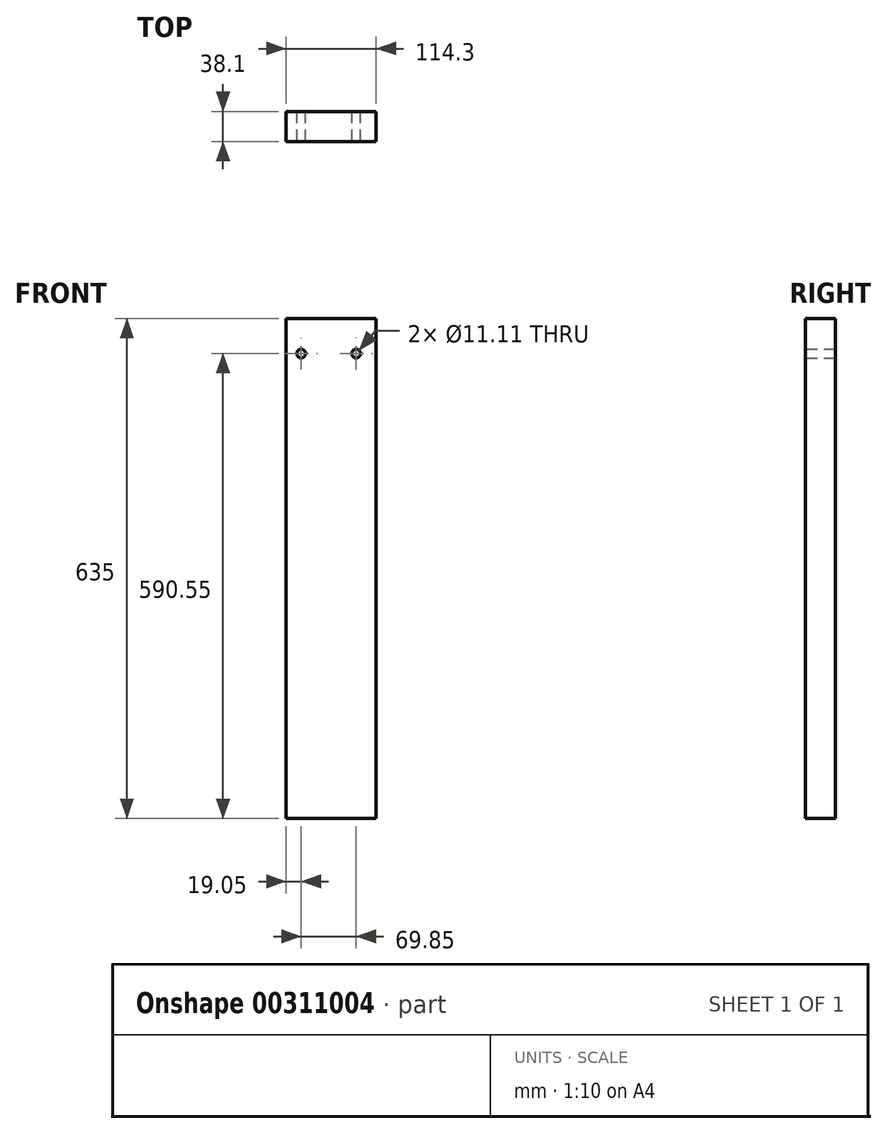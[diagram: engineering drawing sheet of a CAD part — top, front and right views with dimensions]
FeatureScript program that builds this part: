
annotation { "Feature Type Name" : "Feature", "Feature Type Description" : "" }
export const myFeature = defineFeature(function(context is Context, id is Id, definition is map)
    precondition{}
    {
        {
            var Q0;
            Q0=qCreatedBy(makeId("Front.planeOp"),FACE);
            var sketch = newSketch(context, id + "F0", { "sketchPlane" : qUnion([Q0])});
            skLineSegment(sketch, "E0", {"start": v(0, 0) * mm, "end": v(114.3, 0) * mm});
            skLineSegment(sketch, "E1", {"start": v(114.3, 0) * mm, "end": v(114.3, -635) * mm});
            skLineSegment(sketch, "E2", {"start": v(114.3, -635) * mm, "end": v(0, -635) * mm});
            skLineSegment(sketch, "E3", {"start": v(0, -635) * mm, "end": v(0, 0) * mm});
            skSolve(sketch);
        }
        {
            var Q0;
            Q0=makeQuery(id+"F0.imprint","IMPRINT",FACE,{"disambiguationData":[TD([[makeQuery(id+"F0.imprint","IMPRINT",EDGE,{"derivedFrom":sQuery(id+"F0.wireOp",EDGE,"E0")}),-1.0]])]});
            extrude(context, id + "F1", {"entities" : qUnion([Q0]), "oppositeDirection" : true, "depth" : 38.1 * mm});
        }
        {
            var Q0;
            Q0=makeQuery(id+"F1.opExtrude","CAP_FACE",FACE,{"disambiguationData":[OSD([sQuery(id+"F0.wireOp",EDGE,"E0"),sQuery(id+"F0.wireOp",EDGE,"E1"),sQuery(id+"F0.wireOp",EDGE,"E2"),sQuery(id+"F0.wireOp",EDGE,"E3")])],"isStart":true});
            var sketch = newSketch(context, id + "F2", { "sketchPlane" : qUnion([Q0])});
            skLineSegment(sketch, "E4", {"start": v(0, -44.45) * mm, "end": v(114.3, -44.45) * mm, "construction": true});
            skPoint(sketch, "E5", {"position": v(19.05, -44.45) * mm});
            skPoint(sketch, "E6", {"position": v(88.9, -44.45) * mm});
            skSolve(sketch);
        }
        {
            var Q0;
            Q0=sQuery(id+"F2.wireOp",VERTEX,"E5");
            var Q1;
            Q1=sQuery(id+"F2.wireOp",VERTEX,"E6");
            var Q2;
            Q2=makeQuery(id+"F1.opExtrude","SWEPT_BODY",BODY,{"disambiguationData":[OSD([sQuery(id+"F0.wireOp",EDGE,"E0"),sQuery(id+"F0.wireOp",EDGE,"E1"),sQuery(id+"F0.wireOp",EDGE,"E2"),sQuery(id+"F0.wireOp",EDGE,"E3")])]});
            hole(context, id + "F3", {"style" : HoleStyle.SIMPLE, "endStyle" : HoleEndStyle.THROUGH, "holeDiameter" : 11.1 * mm, "tappedDepth" : 12.7 * mm, "tapClearance" : 3, "locations" : qUnion([Q0, Q1]), "scope" : qUnion([Q2])});
        }
    });
